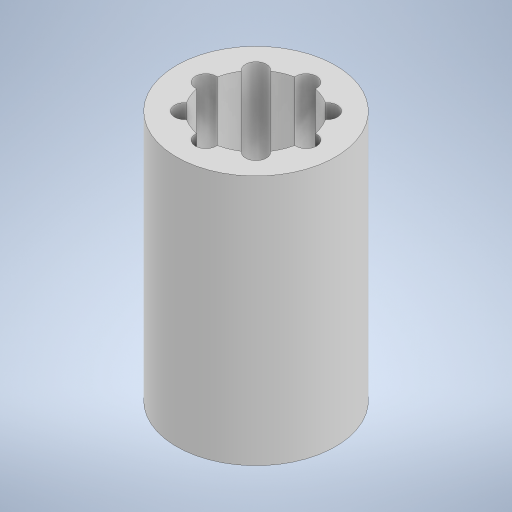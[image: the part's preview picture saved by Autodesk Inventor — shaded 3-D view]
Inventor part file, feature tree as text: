
AUTODESK INVENTOR PART (.ipt)
format: ipt  version: 2023 (Build 270158000, 158)  size: 244,224 bytes
history: native  units: mm
features: extrude x1, sketch x1
ambient origin geometry x8: Origin, YZ Plane, XZ Plane, XY Plane, X Axis, Y Axis, Z Axis, Center Point
bodies: Solid1 (feature_tree)
feature tree (2):
  extrude  "Extrusion1"  Depth=6.0mm
  sketch  "Sketch1"  dims[d0=19.0mm d1=12.0mm d2=2.5mm d3=30.0mm d4=0.0mm d14=6.0mm d15=2.25mm d16=80.0mm d18=360.0deg d20=4.242641mm d21=4.242641mm d22=6.0mm]
